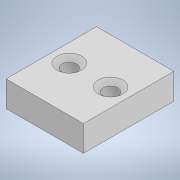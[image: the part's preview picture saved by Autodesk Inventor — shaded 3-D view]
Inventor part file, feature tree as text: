
AUTODESK INVENTOR PART (.ipt)
format: ipt  version: 2021.2 (Build 252289000, 289)  size: 105,472 bytes
history: native  units: in
note: dims shown in document units (in); Inventor stores cm internally (conversion verified against a paired STEP export)
features: sketch x2, extrude x1, hole x1
ambient origin geometry x8: Origin, YZ Plane, XZ Plane, XY Plane, X Axis, Y Axis, Z Axis, Center Point
bodies: Solid1 (feature_tree)
feature tree (4):
  extrude  "Extrusion1"  Depth=0.438in
  hole  "Hole1"  [1 undecoded]
  sketch  "Sketch1"  dims[d0=0.375in d1=0.438in]
  sketch  "Sketch2"  dims[d2=0.125in d3=0.0in d6=0.219in d7=0.07in d8=0.75in d9=0.119in d10=0.25in d11=0.6871in d12=1.0in d13=0.8108in d14=0.219in]
note: 1 required parameter value undecoded (feature->parameter linkage not recoverable at this tier; creation-order binding heuristic only, values carry confidence <= 0.55)
